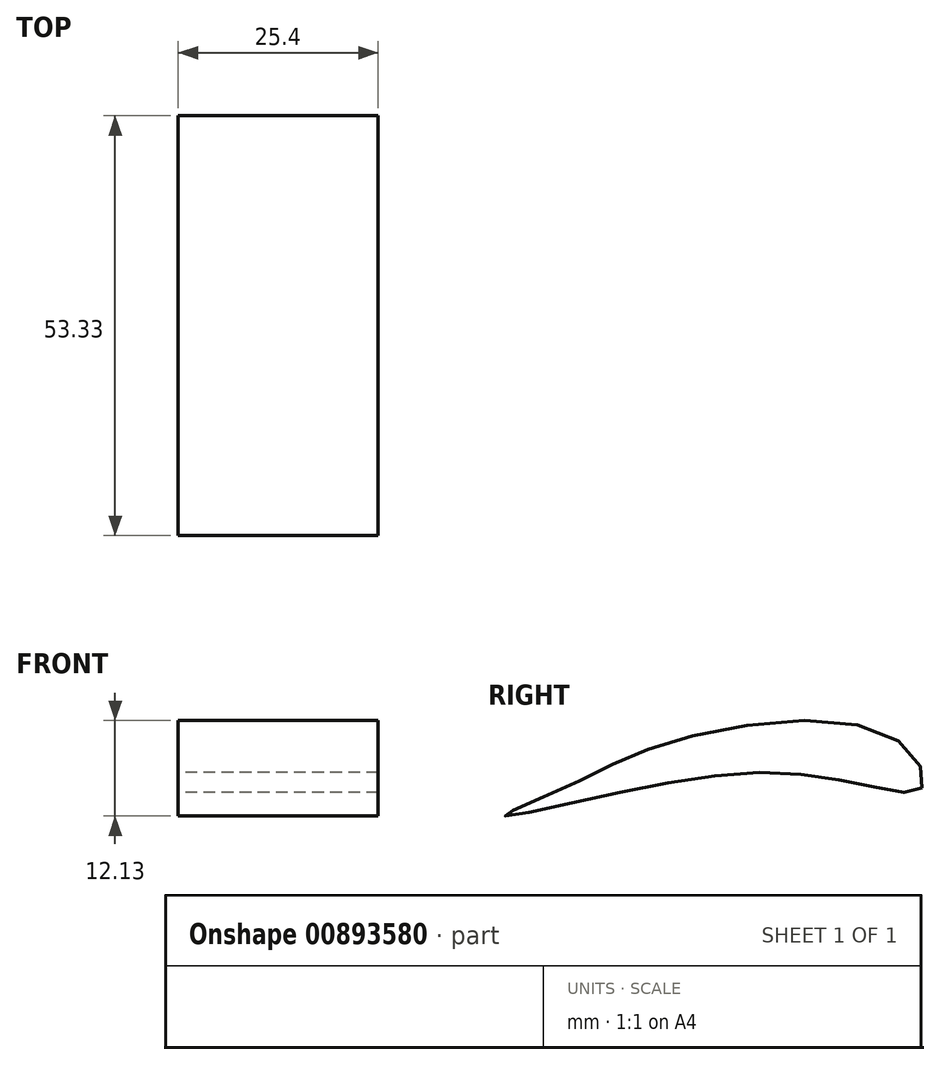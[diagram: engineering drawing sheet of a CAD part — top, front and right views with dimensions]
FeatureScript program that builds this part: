
annotation { "Feature Type Name" : "Feature", "Feature Type Description" : "" }
export const myFeature = defineFeature(function(context is Context, id is Id, definition is map)
    precondition{}
    {
        {
            var Q0;
            Q0=qCreatedBy(makeId("Right.planeOp"),FACE);
            var sketch = newSketch(context, id + "F0", { "sketchPlane" : qUnion([Q0])});
            skFitSpline(sketch, "E0", {"points": [v(25.8, 7.42) * mm, v(22.17, 13.77) * mm, v(-5.08, 13.57) * mm, v(-19.61, 7.42) * mm, v(-27.29, 3.88) * mm, v(-16.79, 5.9) * mm, v(5.62, 9.33) * mm, v(20.15, 7.42) * mm, v(25.8, 7.42) * mm]});
            skSolve(sketch);
        }
        {
            var Q0;
            Q0=makeQuery(id+"F0.imprint","IMPRINT",FACE,{"disambiguationData":[TD([[makeQuery(id+"F0.imprint","IMPRINT",EDGE,{"derivedFrom":sQuery(id+"F0.wireOp",EDGE,"E0")}),1.0]])]});
            extrude(context, id + "F1", {"entities" : qUnion([Q0]), "depth" : 25.4 * mm, "offsetDistance" : 25.4 * mm});
        }
    });
